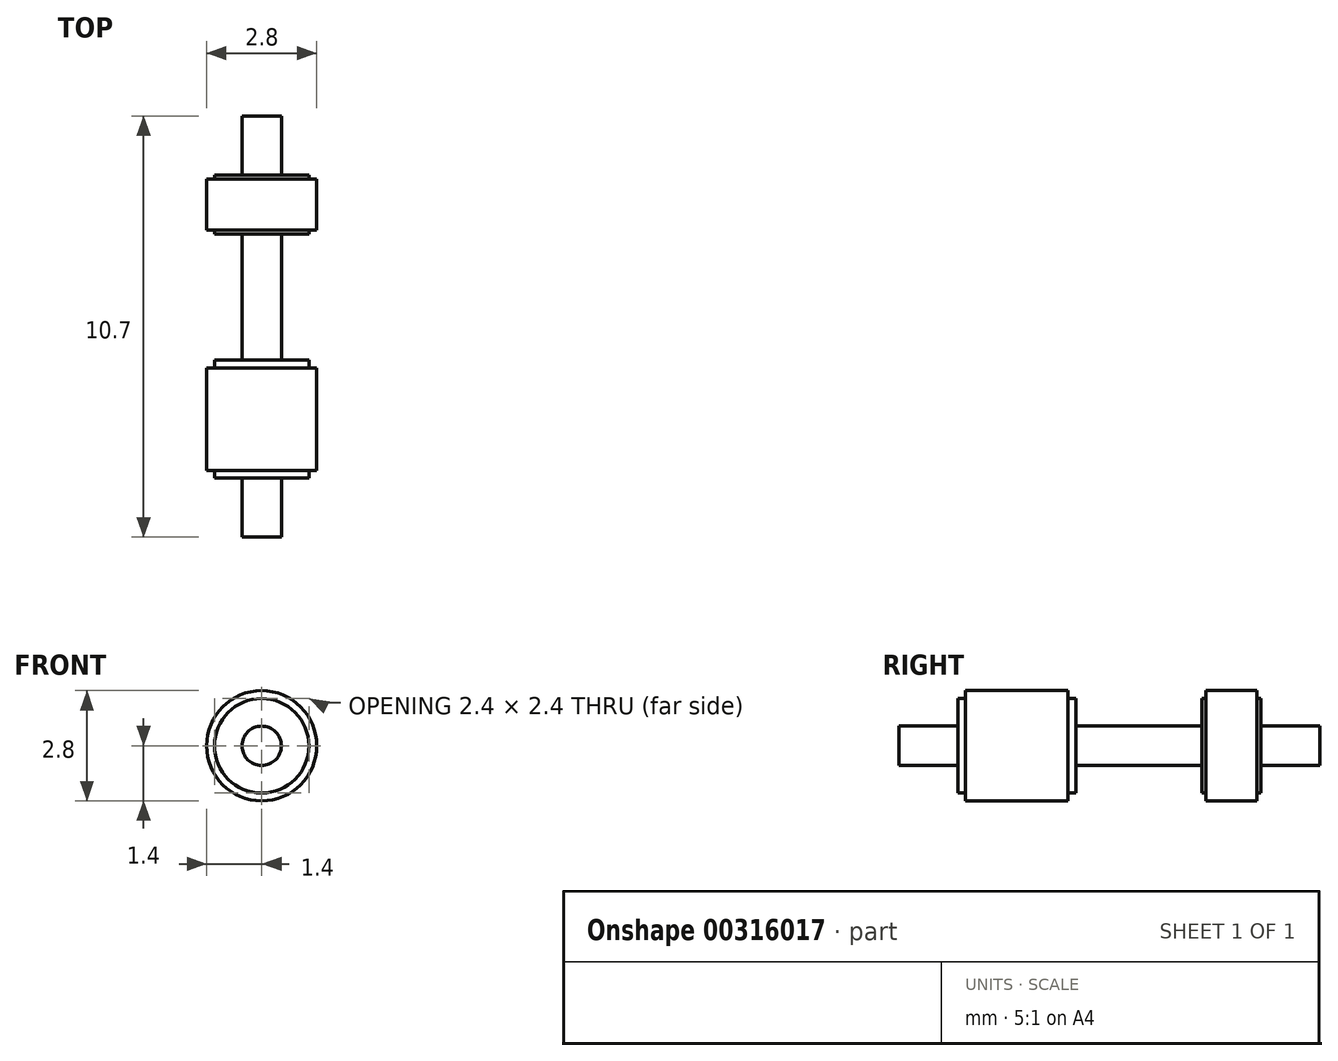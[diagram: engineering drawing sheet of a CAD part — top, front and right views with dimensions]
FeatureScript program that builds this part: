
annotation { "Feature Type Name" : "Feature", "Feature Type Description" : "" }
export const myFeature = defineFeature(function(context is Context, id is Id, definition is map)
    precondition{}
    {
        {
            var Q0;
            Q0=qCreatedBy(makeId("Right.planeOp"),FACE);
            var sketch = newSketch(context, id + "F0", { "sketchPlane" : qUnion([Q0])});
            skLineSegment(sketch, "E0", {"start": v(-1.5, 0) * mm, "end": v(-1.5, 0.5) * mm});
            skLineSegment(sketch, "E1", {"start": v(-1.5, 0.5) * mm, "end": v(0, 0.5) * mm});
            skLineSegment(sketch, "E2", {"start": v(0, 0.5) * mm, "end": v(0, 1.4) * mm});
            skLineSegment(sketch, "E3", {"start": v(0, 1.4) * mm, "end": v(3, 1.4) * mm});
            skLineSegment(sketch, "E4", {"start": v(3, 1.4) * mm, "end": v(3, 0.5) * mm});
            skLineSegment(sketch, "E5", {"start": v(3, 0.5) * mm, "end": v(6.2, 0.5) * mm});
            skLineSegment(sketch, "E6", {"start": v(6.2, 0.5) * mm, "end": v(6.2, 1.2) * mm});
            skLineSegment(sketch, "E7", {"start": v(6.2, 1.2) * mm, "end": v(7.7, 1.2) * mm});
            skLineSegment(sketch, "E8", {"start": v(7.7, 1.2) * mm, "end": v(7.7, 0.5) * mm});
            skLineSegment(sketch, "E9", {"start": v(7.7, 0.5) * mm, "end": v(9.2, 0.5) * mm});
            skLineSegment(sketch, "E10", {"start": v(9.2, 0.5) * mm, "end": v(9.2, 0) * mm});
            skLineSegment(sketch, "E11", {"start": v(9.2, 0) * mm, "end": v(-1.5, 0) * mm});
            skSolve(sketch);
        }
        {
            var Q0;
            Q0 = qSketchRegion(id + "F0", true);
            var Q1;
            Q1=sQuery(id+"F0.wireOp",EDGE,"E11");
            revolve(context, id + "F1", {"surfaceOperationType" : NewSurfaceOperationType.NEW, "entities" : qUnion([Q0]), "axis" : qUnion([Q1]), "revolveType" : RevolveType.FULL});
        }
        {
            var Q0;
            Q0=qCreatedBy(makeId("Right.planeOp"),FACE);
            var sketch = newSketch(context, id + "F2", { "sketchPlane" : qUnion([Q0])});
            skLineSegment(sketch, "E12.0", {"start": v(3, 1.4) * mm, "end": v(3, -1.4) * mm});
            skLineSegment(sketch, "E13", {"start": v(0, 1.4) * mm, "end": v(3, 1.4) * mm});
            skLineSegment(sketch, "E14.0", {"start": v(0, 1.4) * mm, "end": v(0, -1.4) * mm});
            skLineSegment(sketch, "E15.bottom", {"start": v(0, 1.4) * mm, "end": v(0.2, 1.4) * mm});
            skLineSegment(sketch, "E15.top", {"start": v(0, 1.2) * mm, "end": v(0.2, 1.2) * mm});
            skLineSegment(sketch, "E15.left", {"start": v(0, 1.4) * mm, "end": v(0, 1.2) * mm});
            skLineSegment(sketch, "E15.right", {"start": v(0.2, 1.4) * mm, "end": v(0.2, 1.2) * mm});
            skLineSegment(sketch, "E16.bottom", {"start": v(3, 1.4) * mm, "end": v(2.8, 1.4) * mm});
            skLineSegment(sketch, "E16.top", {"start": v(3, 1.2) * mm, "end": v(2.8, 1.2) * mm});
            skLineSegment(sketch, "E16.left", {"start": v(3, 1.4) * mm, "end": v(3, 1.2) * mm});
            skLineSegment(sketch, "E16.right", {"start": v(2.8, 1.4) * mm, "end": v(2.8, 1.2) * mm});
            skLineSegment(sketch, "E17", {"start": v(0, 0) * mm, "end": v(3, 0) * mm, "construction": true});
            skSolve(sketch);
        }
        {
            var Q0;
            Q0 = qSketchRegion(id + "F2", true);
            var Q1;
            Q1=sQuery(id+"F2.wireOp",EDGE,"E17");
            revolve(context, id + "F3", {"operationType" : NewBodyOperationType.REMOVE, "surfaceOperationType" : NewSurfaceOperationType.NEW, "entities" : qUnion([Q0]), "axis" : qUnion([Q1]), "revolveType" : RevolveType.FULL, "oppositeDirection" : true});
        }
        {
            var Q0;
            Q0=qCreatedBy(makeId("Right.planeOp"),FACE);
            var sketch = newSketch(context, id + "F4", { "sketchPlane" : qUnion([Q0])});
            skLineSegment(sketch, "E18", {"start": v(6.7, 1.2) * mm, "end": v(7.7, 1.2) * mm});
            skLineSegment(sketch, "E19.0", {"start": v(6.2, 1.2) * mm, "end": v(6.2, -1.2) * mm});
            skLineSegment(sketch, "E20.0", {"start": v(7.7, 1.2) * mm, "end": v(7.7, -1.2) * mm});
            skLineSegment(sketch, "E21.bottom", {"start": v(6.3, 1.2) * mm, "end": v(7.6, 1.2) * mm});
            skLineSegment(sketch, "E21.top", {"start": v(6.3, 1.4) * mm, "end": v(7.6, 1.4) * mm});
            skLineSegment(sketch, "E21.left", {"start": v(6.3, 1.2) * mm, "end": v(6.3, 1.4) * mm});
            skLineSegment(sketch, "E21.right", {"start": v(7.6, 1.2) * mm, "end": v(7.6, 1.4) * mm});
            skLineSegment(sketch, "E22", {"start": v(6.2, 0) * mm, "end": v(7.7, 0) * mm, "construction": true});
            skSolve(sketch);
        }
        {
            var Q0;
            Q0 = qSketchRegion(id + "F4", true);
            var Q1;
            Q1=sQuery(id+"F4.wireOp",EDGE,"E22");
            revolve(context, id + "F5", {"operationType" : NewBodyOperationType.ADD, "surfaceOperationType" : NewSurfaceOperationType.NEW, "entities" : qUnion([Q0]), "axis" : qUnion([Q1]), "revolveType" : RevolveType.FULL});
        }
    });
